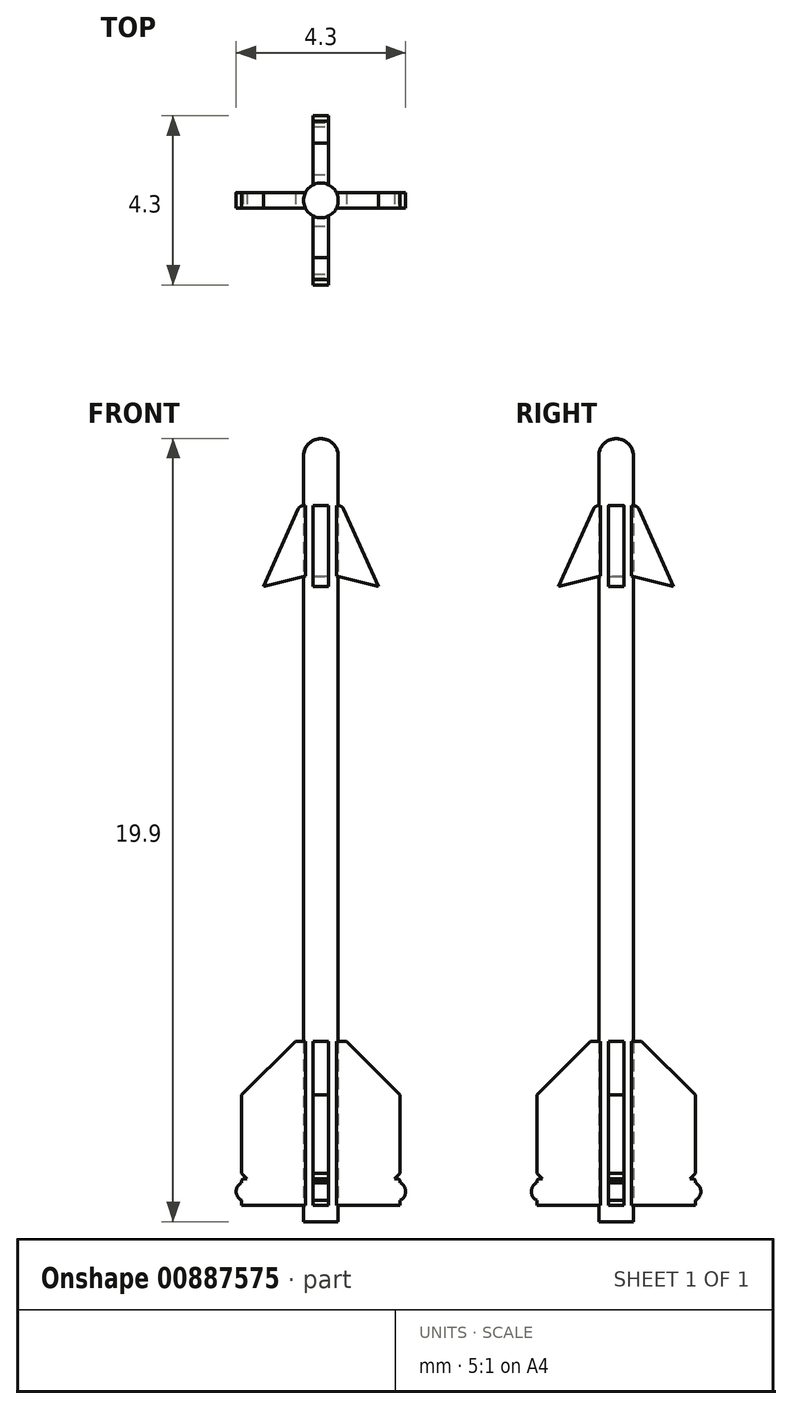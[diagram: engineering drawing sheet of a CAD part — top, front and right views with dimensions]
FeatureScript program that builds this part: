
annotation { "Feature Type Name" : "Feature", "Feature Type Description" : "" }
export const myFeature = defineFeature(function(context is Context, id is Id, definition is map)
    precondition{}
    {
        {
            var Q0;
            Q0=qCreatedBy(makeId("Front.planeOp"),FACE);
            var sketch = newSketch(context, id + "F0", { "sketchPlane" : qUnion([Q0])});
            skLineSegment(sketch, "E0", {"start": v(0, 0) * mm, "end": v(0, 19.9) * mm});
            skLineSegment(sketch, "E1", {"start": v(0.44, 19.45) * mm, "end": v(0.44, 0) * mm});
            skLineSegment(sketch, "E2", {"start": v(0.44, 0) * mm, "end": v(0, 0) * mm});
            skArc(sketch, "E3", {"start": v(0.44, 19.45) * mm, "mid": v(0.31, 19.77) * mm, "end": v(0, 19.9) * mm});
            skLineSegment(sketch, "E4", {"start": v(0, 19.9) * mm, "end": v(1.85, 19.9) * mm, "construction": true});
            skSolve(sketch);
        }
        {
            var Q0;
            Q0=qSketchRegion(id+"F0",true);
            var Q1;
            Q1=sQuery(id+"F0.wireOp",EDGE,"E0");
            revolve(context, id + "F1", {"surfaceOperationType" : NewSurfaceOperationType.NEW, "entities" : qUnion([Q0]), "axis" : qUnion([Q1]), "revolveType" : RevolveType.FULL});
        }
        {
            var Q0;
            Q0=qCreatedBy(makeId("Front.planeOp"),FACE);
            var sketch = newSketch(context, id + "F2", { "sketchPlane" : qUnion([Q0])});
            skLineSegment(sketch, "E5", {"start": v(0.65, 4.58) * mm, "end": v(-0.65, 4.58) * mm});
            skLineSegment(sketch, "E6", {"start": v(-2.01, 3.23) * mm, "end": v(-0.65, 4.58) * mm});
            skLineSegment(sketch, "E7", {"start": v(-2.01, 3.23) * mm, "end": v(-2.01, 1.23) * mm});
            skLineSegment(sketch, "E8", {"start": v(2.01, 1.23) * mm, "end": v(2.01, 3.23) * mm});
            skLineSegment(sketch, "E9", {"start": v(0.65, 4.58) * mm, "end": v(2.01, 3.23) * mm});
            skLineSegment(sketch, "E10", {"start": v(0, 0) * mm, "end": v(0, 4.58) * mm, "construction": true});
            skLineSegment(sketch, "E11", {"start": v(-0.44, 0.8) * mm, "end": v(-0.44, 4.16) * mm, "construction": true});
            skLineSegment(sketch, "E12.0", {"start": v(0.44, 19.45) * mm, "end": v(-0.44, 19.45) * mm});
            skLineSegment(sketch, "E13", {"start": v(-2.01, 0.42) * mm, "end": v(-2.01, 0.54) * mm});
            skLineSegment(sketch, "E14", {"start": v(2.01, 0.42) * mm, "end": v(2.01, 0.54) * mm});
            skLineSegment(sketch, "E15", {"start": v(2.01, 1.23) * mm, "end": v(1.88, 1.1) * mm});
            skLineSegment(sketch, "E16", {"start": v(2.01, 1.05) * mm, "end": v(2.01, 1) * mm});
            skLineSegment(sketch, "E17", {"start": v(-2.01, 1.23) * mm, "end": v(-1.88, 1.1) * mm});
            skLineSegment(sketch, "E18", {"start": v(-2.01, 1.05) * mm, "end": v(-2.01, 1) * mm});
            skArc(sketch, "E19", {"start": v(-2.01, 1) * mm, "mid": v(-2.15, 0.77) * mm, "end": v(-2.01, 0.54) * mm});
            skArc(sketch, "E20", {"start": v(2.01, 0.54) * mm, "mid": v(2.15, 0.77) * mm, "end": v(2.01, 1) * mm});
            skLineSegment(sketch, "E21", {"start": v(-2.01, 1.05) * mm, "end": v(-1.97, 1.1) * mm});
            skLineSegment(sketch, "E22", {"start": v(-1.97, 1.1) * mm, "end": v(-1.88, 1.1) * mm});
            skLineSegment(sketch, "E23", {"start": v(2.01, 1.05) * mm, "end": v(1.97, 1.1) * mm});
            skLineSegment(sketch, "E24", {"start": v(1.97, 1.1) * mm, "end": v(1.88, 1.1) * mm});
            skLineSegment(sketch, "E25", {"start": v(-2.01, 0.42) * mm, "end": v(2.01, 0.42) * mm});
            skLineSegment(sketch, "E26", {"start": v(0, 0) * mm, "end": v(0, 0.42) * mm, "construction": true});
            skLineSegment(sketch, "E27.0", {"start": v(0.44, 0) * mm, "end": v(-0.44, 0) * mm});
            skLineSegment(sketch, "E28", {"start": v(-1.46, 16.15) * mm, "end": v(0, 16.5) * mm});
            skLineSegment(sketch, "E29", {"start": v(0, 16.5) * mm, "end": v(1.46, 16.15) * mm});
            skLineSegment(sketch, "E30", {"start": v(1.46, 16.15) * mm, "end": v(0.58, 18.1) * mm});
            skLineSegment(sketch, "E31", {"start": v(-0.58, 18.1) * mm, "end": v(-1.46, 16.15) * mm});
            skLineSegment(sketch, "E32", {"start": v(-0.44, 18.2) * mm, "end": v(0.44, 18.2) * mm});
            skArc(sketch, "E33", {"start": v(-0.44, 18.2) * mm, "mid": v(-0.52, 18.17) * mm, "end": v(-0.58, 18.1) * mm});
            skArc(sketch, "E34", {"start": v(0.58, 18.1) * mm, "mid": v(0.52, 18.17) * mm, "end": v(0.44, 18.2) * mm});
            skPoint(sketch, "E35", {"position": v(-0.44, 16.39) * mm});
            skSolve(sketch);
        }
        {
            var Q0;
            Q0=qSketchRegion(id+"F2",true);
            extrude(context, id + "F3", {"entities" : qUnion([Q0]), "operationType" : NewBodyOperationType.ADD, "depth" : .4 * mm, "offsetDistance" : 25 * mm, "symmetric" : true});
        }
        {
            var Q0;
            Q0=makeQuery(id+"F1.opRevolve","SWEPT_BODY",BODY,{"disambiguationData":[OSD([sQuery(id+"F0.wireOp",EDGE,"E0"),sQuery(id+"F0.wireOp",EDGE,"E1"),sQuery(id+"F0.wireOp",EDGE,"E2"),sQuery(id+"F0.wireOp",EDGE,"E3")])]});
            var Q1;
            Q1=makeQuery(id+"F1.opRevolve","SWEPT_FACE",FACE,{"disambiguationData":[OSD([sQuery(id+"F0.wireOp",EDGE,"E1")])]});
            circularPattern(context, id + "F4", {"entities" : qUnion([Q0]), "axis" : qUnion([Q1]), "angle" : 360 * degree, "instanceCount" : 4, "equalSpace" : true, "computeTransformsWithoutBuiltin" : true});
        }
    });
